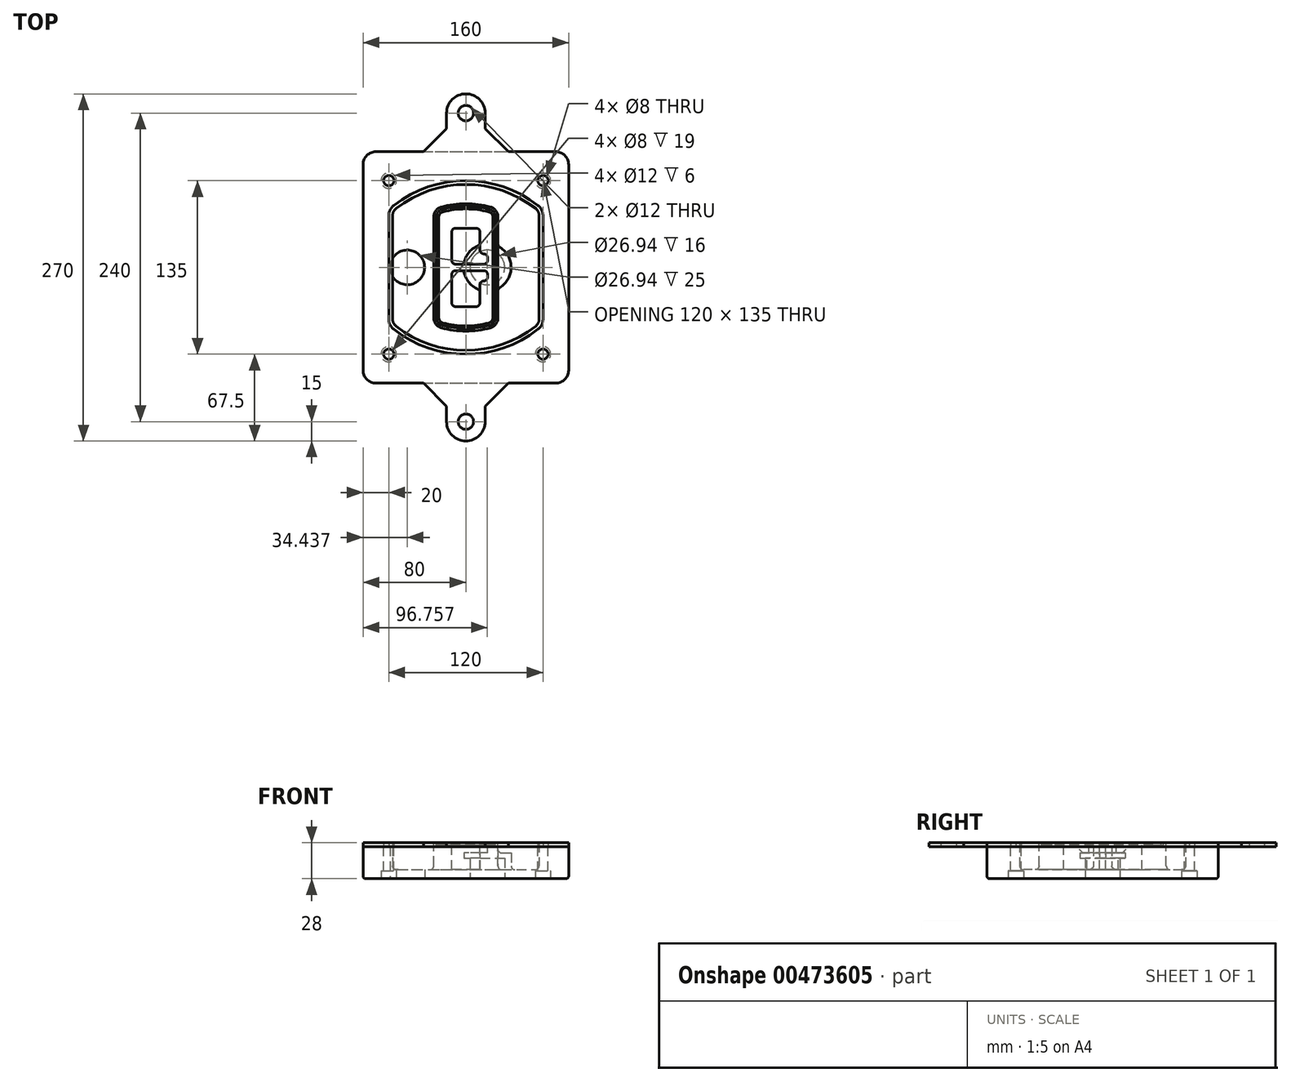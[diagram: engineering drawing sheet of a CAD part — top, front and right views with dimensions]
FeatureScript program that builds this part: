
annotation { "Feature Type Name" : "Feature", "Feature Type Description" : "" }
export const myFeature = defineFeature(function(context is Context, id is Id, definition is map)
    precondition{}
    {
        {
            var Q0;
            Q0=qCreatedBy(makeId("Top.planeOp"),FACE);
            var sketch = newSketch(context, id + "F0", { "sketchPlane" : qUnion([Q0])});
            skPoint(sketch, "E0.rect.middle", {"position": v(0, 0) * mm});
            skLineSegment(sketch, "E1.bottom", {"start": v(-70, -90) * mm, "end": v(70, -90) * mm});
            skLineSegment(sketch, "E1.top", {"start": v(-70, 90) * mm, "end": v(70, 90) * mm});
            skLineSegment(sketch, "E1.left", {"start": v(-80, -80) * mm, "end": v(-80, 80) * mm});
            skLineSegment(sketch, "E1.right", {"start": v(80, -80) * mm, "end": v(80, 80) * mm});
            skLineSegment(sketch, "E2", {"start": v(-80, 90) * mm, "end": v(80, -90) * mm, "construction": true});
            skLineSegment(sketch, "E3", {"start": v(80, 90) * mm, "end": v(-80, -90) * mm, "construction": true});
            skCircle(sketch, "E4", {"center": v(-60, 67.5) * mm, "radius": 4 * mm});
            skCircle(sketch, "E5", {"center": v(60, 67.5) * mm, "radius": 4 * mm});
            skCircle(sketch, "E6", {"center": v(60, -67.5) * mm, "radius": 4 * mm});
            skCircle(sketch, "E7", {"center": v(-60, -67.5) * mm, "radius": 4 * mm});
            skLineSegment(sketch, "E8", {"start": v(-60, 67.5) * mm, "end": v(60, 67.5) * mm, "construction": true});
            skLineSegment(sketch, "E9", {"start": v(60, 67.5) * mm, "end": v(60, -67.5) * mm, "construction": true});
            skLineSegment(sketch, "E10", {"start": v(60, -67.5) * mm, "end": v(-60, -67.5) * mm, "construction": true});
            skLineSegment(sketch, "E11", {"start": v(-60, -67.5) * mm, "end": v(-60, 67.5) * mm, "construction": true});
            skLineSegment(sketch, "E12", {"start": v(-60, 40.3) * mm, "end": v(-60, -40.3) * mm});
            skLineSegment(sketch, "E13", {"start": v(60, 40.3) * mm, "end": v(60, -40.3) * mm});
            skArc(sketch, "E14", {"start": v(56.15, 48.18) * mm, "mid": v(0, 67.5) * mm, "end": v(-56.15, 48.18) * mm});
            skArc(sketch, "E15", {"start": v(-56.15, -48.18) * mm, "mid": v(0, -67.5) * mm, "end": v(56.15, -48.18) * mm});
            skLineSegment(sketch, "E16", {"start": v(-60, 0) * mm, "end": v(60, 0) * mm, "construction": true});
            skPoint(sketch, "E17.visualSharp", {"position": v(-60, -45) * mm});
            skArc(sketch, "E17.filletArc", {"start": v(-60, -40.3) * mm, "mid": v(-58.99, -44.68) * mm, "end": v(-56.15, -48.18) * mm});
            skPoint(sketch, "E18.visualSharp", {"position": v(-60, 45) * mm});
            skArc(sketch, "E18.filletArc", {"start": v(-56.15, 48.18) * mm, "mid": v(-58.99, 44.68) * mm, "end": v(-60, 40.3) * mm});
            skPoint(sketch, "E19.visualSharp", {"position": v(60, 45) * mm});
            skArc(sketch, "E19.filletArc", {"start": v(60, 40.3) * mm, "mid": v(58.99, 44.68) * mm, "end": v(56.15, 48.18) * mm});
            skPoint(sketch, "E20.visualSharp", {"position": v(60, -45) * mm});
            skArc(sketch, "E20.filletArc", {"start": v(56.15, -48.18) * mm, "mid": v(58.99, -44.68) * mm, "end": v(60, -40.3) * mm});
            skPoint(sketch, "E21.visualSharp", {"position": v(-80, 90) * mm});
            skArc(sketch, "E21.filletArc", {"start": v(-70, 90) * mm, "mid": v(-77.07, 87.07) * mm, "end": v(-80, 80) * mm});
            skPoint(sketch, "E22.visualSharp", {"position": v(80, 90) * mm});
            skArc(sketch, "E22.filletArc", {"start": v(80, 80) * mm, "mid": v(77.07, 87.07) * mm, "end": v(70, 90) * mm});
            skPoint(sketch, "E23.visualSharp", {"position": v(80, -90) * mm});
            skArc(sketch, "E23.filletArc", {"start": v(70, -90) * mm, "mid": v(77.07, -87.07) * mm, "end": v(80, -80) * mm});
            skPoint(sketch, "E24.visualSharp", {"position": v(-80, -90) * mm});
            skArc(sketch, "E24.filletArc", {"start": v(-80, -80) * mm, "mid": v(-77.07, -87.07) * mm, "end": v(-70, -90) * mm});
            skArc(sketch, "E25.0", {"start": v(57, 40.3) * mm, "mid": v(56.3, 43.36) * mm, "end": v(54.3, 45.81) * mm});
            skLineSegment(sketch, "E25.1", {"start": v(57, 40.3) * mm, "end": v(57, -40.3) * mm});
            skArc(sketch, "E25.2", {"start": v(54.3, -45.81) * mm, "mid": v(56.3, -43.36) * mm, "end": v(57, -40.3) * mm});
            skArc(sketch, "E25.3", {"start": v(-54.3, -45.81) * mm, "mid": v(0, -64.5) * mm, "end": v(54.3, -45.81) * mm});
            skArc(sketch, "E25.4", {"start": v(-57, -40.3) * mm, "mid": v(-56.3, -43.36) * mm, "end": v(-54.3, -45.81) * mm});
            skArc(sketch, "E25.5", {"start": v(54.3, 45.81) * mm, "mid": v(0, 64.5) * mm, "end": v(-54.3, 45.81) * mm});
            skLineSegment(sketch, "E25.6", {"start": v(-57, 40.3) * mm, "end": v(-57, -40.3) * mm});
            skArc(sketch, "E25.7", {"start": v(-54.3, 45.81) * mm, "mid": v(-56.3, 43.36) * mm, "end": v(-57, 40.3) * mm});
            skArc(sketch, "E26.0", {"start": v(-58.62, 51.33) * mm, "mid": v(-62.58, 46.43) * mm, "end": v(-64, 40.3) * mm});
            skArc(sketch, "E26.1", {"start": v(58.62, 51.33) * mm, "mid": v(0, 71.5) * mm, "end": v(-58.62, 51.33) * mm});
            skArc(sketch, "E26.2", {"start": v(64, 40.3) * mm, "mid": v(62.58, 46.43) * mm, "end": v(58.62, 51.33) * mm});
            skLineSegment(sketch, "E26.3", {"start": v(64, 40.3) * mm, "end": v(64, -40.3) * mm});
            skArc(sketch, "E26.4", {"start": v(58.62, -51.33) * mm, "mid": v(62.58, -46.43) * mm, "end": v(64, -40.3) * mm});
            skLineSegment(sketch, "E26.5", {"start": v(-64, 40.3) * mm, "end": v(-64, -40.3) * mm});
            skArc(sketch, "E26.6", {"start": v(-58.62, -51.33) * mm, "mid": v(0, -71.5) * mm, "end": v(58.62, -51.33) * mm});
            skArc(sketch, "E26.7", {"start": v(-64, -40.3) * mm, "mid": v(-62.58, -46.43) * mm, "end": v(-58.62, -51.33) * mm});
            skSolve(sketch);
        }
        {
            var Q0;
            Q0=makeQuery(id+"F0.imprint","IMPRINT",FACE,{"disambiguationData":[TD([[makeQuery(id+"F0.imprint","IMPRINT",EDGE,{"derivedFrom":sQuery(id+"F0.wireOp",EDGE,"E1.bottom")}),1.0]])]});
            var Q1;
            Q1=makeQuery(id+"F0.imprint","IMPRINT",FACE,{"disambiguationData":[TD([[makeQuery(id+"F0.imprint","IMPRINT",EDGE,{"derivedFrom":sQuery(id+"F0.wireOp",EDGE,"E12")}),1.0]])]});
            var Q2;
            Q2=makeQuery(id+"F0.imprint","IMPRINT",FACE,{"disambiguationData":[TD([[makeQuery(id+"F0.imprint","IMPRINT",EDGE,{"derivedFrom":sQuery(id+"F0.wireOp",EDGE,"E25.0")}),1.0]])]});
            var Q3;
            Q3=makeQuery(id+"F0.imprint","IMPRINT",FACE,{"disambiguationData":[TD([[makeQuery(id+"F0.imprint","IMPRINT",EDGE,{"derivedFrom":sQuery(id+"F0.wireOp",EDGE,"E12")}),-1.0]])]});
            extrude(context, id + "F1", {"entities" : qUnion([Q0, Q1, Q2, Q3]), "oppositeDirection" : true, "depth" : 25 * mm});
        }
        {
            var Q0;
            Q0=makeQuery(id+"F0.imprint","IMPRINT",FACE,{"disambiguationData":[TD([[makeQuery(id+"F0.imprint","IMPRINT",EDGE,{"derivedFrom":sQuery(id+"F0.wireOp",EDGE,"E12")}),1.0]])]});
            extrude(context, id + "F2", {"entities" : qUnion([Q0]), "operationType" : NewBodyOperationType.ADD, "depth" : 3 * mm});
        }
        {
            var Q0;
            Q0=makeQuery(id+"F0.imprint","IMPRINT",FACE,{"disambiguationData":[TD([[makeQuery(id+"F0.imprint","IMPRINT",EDGE,{"derivedFrom":sQuery(id+"F0.wireOp",EDGE,"E25.0")}),1.0]])]});
            extrude(context, id + "F3", {"entities" : qUnion([Q0]), "operationType" : NewBodyOperationType.REMOVE, "oppositeDirection" : true, "depth" : 18 * mm});
        }
        {
            var Q0;
            Q0=makeQuery(id+"F2.opExtrude","CAP_FACE",FACE,{"disambiguationData":[OSD([sQuery(id+"F0.wireOp",EDGE,"E12"),sQuery(id+"F0.wireOp",EDGE,"E13"),sQuery(id+"F0.wireOp",EDGE,"E14"),sQuery(id+"F0.wireOp",EDGE,"E15"),sQuery(id+"F0.wireOp",EDGE,"E17.filletArc"),sQuery(id+"F0.wireOp",EDGE,"E18.filletArc"),sQuery(id+"F0.wireOp",EDGE,"E19.filletArc"),sQuery(id+"F0.wireOp",EDGE,"E20.filletArc"),sQuery(id+"F0.wireOp",EDGE,"E25.0"),sQuery(id+"F0.wireOp",EDGE,"E25.1"),sQuery(id+"F0.wireOp",EDGE,"E25.2"),sQuery(id+"F0.wireOp",EDGE,"E25.3"),sQuery(id+"F0.wireOp",EDGE,"E25.4"),sQuery(id+"F0.wireOp",EDGE,"E25.5"),sQuery(id+"F0.wireOp",EDGE,"E25.6"),sQuery(id+"F0.wireOp",EDGE,"E25.7")])],"isStart":false});
            var sketch = newSketch(context, id + "F4", { "sketchPlane" : qUnion([Q0])});
            skArc(sketch, "E27.0", {"start": v(-19.08, -46.97) * mm, "mid": v(0, -49.5) * mm, "end": v(19.08, -46.97) * mm});
            skArc(sketch, "E28.0", {"start": v(19.08, 46.97) * mm, "mid": v(0, 49.5) * mm, "end": v(-19.08, 46.97) * mm});
            skLineSegment(sketch, "E29", {"start": v(-25, 39.25) * mm, "end": v(-25, -39.25) * mm});
            skLineSegment(sketch, "E30", {"start": v(25, 39.25) * mm, "end": v(25, -39.25) * mm});
            skLineSegment(sketch, "E31", {"start": v(-25, 45.1) * mm, "end": v(25, 45.1) * mm, "construction": true});
            skLineSegment(sketch, "E32", {"start": v(-25, -45.1) * mm, "end": v(25, -45.1) * mm, "construction": true});
            skPoint(sketch, "E33.visualSharp", {"position": v(-25, 45.1) * mm});
            skArc(sketch, "E33.filletArc", {"start": v(-19.08, 46.97) * mm, "mid": v(-23.35, 44.11) * mm, "end": v(-25, 39.25) * mm});
            skPoint(sketch, "E34.visualSharp", {"position": v(25, 45.1) * mm});
            skArc(sketch, "E34.filletArc", {"start": v(25, 39.25) * mm, "mid": v(23.35, 44.11) * mm, "end": v(19.08, 46.97) * mm});
            skPoint(sketch, "E35.visualSharp", {"position": v(25, -45.1) * mm});
            skArc(sketch, "E35.filletArc", {"start": v(19.08, -46.97) * mm, "mid": v(23.35, -44.11) * mm, "end": v(25, -39.25) * mm});
            skPoint(sketch, "E36.visualSharp", {"position": v(-25, -45.1) * mm});
            skArc(sketch, "E36.filletArc", {"start": v(-25, -39.25) * mm, "mid": v(-23.35, -44.11) * mm, "end": v(-19.08, -46.97) * mm});
            skArc(sketch, "E37.0", {"start": v(54.3, 45.81) * mm, "mid": v(0, 64.5) * mm, "end": v(-54.3, 45.81) * mm});
            skArc(sketch, "E37.1", {"start": v(-54.3, 45.81) * mm, "mid": v(-56.3, 43.36) * mm, "end": v(-57, 40.3) * mm});
            skLineSegment(sketch, "E37.2", {"start": v(-57, 40.3) * mm, "end": v(-57, -40.3) * mm});
            skArc(sketch, "E37.3", {"start": v(-57, -40.3) * mm, "mid": v(-56.3, -43.36) * mm, "end": v(-54.3, -45.81) * mm});
            skArc(sketch, "E37.4", {"start": v(-54.3, -45.81) * mm, "mid": v(0, -64.5) * mm, "end": v(54.3, -45.81) * mm});
            skArc(sketch, "E37.5", {"start": v(54.3, -45.81) * mm, "mid": v(56.3, -43.36) * mm, "end": v(57, -40.3) * mm});
            skLineSegment(sketch, "E37.6", {"start": v(57, 40.3) * mm, "end": v(57, -40.3) * mm});
            skArc(sketch, "E37.7", {"start": v(57, 40.3) * mm, "mid": v(56.3, 43.36) * mm, "end": v(54.3, 45.81) * mm});
            skLineSegment(sketch, "E38.0", {"start": v(23, 39.25) * mm, "end": v(23, -39.25) * mm});
            skArc(sketch, "E38.1", {"start": v(18.56, -45.04) * mm, "mid": v(21.76, -42.9) * mm, "end": v(23, -39.25) * mm});
            skArc(sketch, "E38.2", {"start": v(-18.56, -45.04) * mm, "mid": v(0, -47.5) * mm, "end": v(18.56, -45.04) * mm});
            skArc(sketch, "E38.3", {"start": v(-23, -39.25) * mm, "mid": v(-21.76, -42.9) * mm, "end": v(-18.56, -45.04) * mm});
            skLineSegment(sketch, "E38.4", {"start": v(-23, 39.25) * mm, "end": v(-23, -39.25) * mm});
            skArc(sketch, "E38.5", {"start": v(23, 39.25) * mm, "mid": v(21.76, 42.9) * mm, "end": v(18.56, 45.04) * mm});
            skArc(sketch, "E38.6", {"start": v(-18.56, 45.04) * mm, "mid": v(-21.76, 42.9) * mm, "end": v(-23, 39.25) * mm});
            skArc(sketch, "E38.7", {"start": v(18.56, 45.04) * mm, "mid": v(0, 47.5) * mm, "end": v(-18.56, 45.04) * mm});
            skArc(sketch, "E39.0", {"start": v(21, 39.25) * mm, "mid": v(20.18, 41.68) * mm, "end": v(18.04, 43.1) * mm});
            skLineSegment(sketch, "E39.1", {"start": v(21, 39.25) * mm, "end": v(21, -39.25) * mm});
            skArc(sketch, "E39.2", {"start": v(18.04, -43.1) * mm, "mid": v(20.18, -41.68) * mm, "end": v(21, -39.25) * mm});
            skArc(sketch, "E39.3", {"start": v(-18.04, -43.1) * mm, "mid": v(0, -45.5) * mm, "end": v(18.04, -43.1) * mm});
            skArc(sketch, "E39.4", {"start": v(-21, -39.25) * mm, "mid": v(-20.18, -41.68) * mm, "end": v(-18.04, -43.1) * mm});
            skArc(sketch, "E39.5", {"start": v(18.04, 43.1) * mm, "mid": v(0, 45.5) * mm, "end": v(-18.04, 43.1) * mm});
            skLineSegment(sketch, "E39.6", {"start": v(-21, 39.25) * mm, "end": v(-21, -39.25) * mm});
            skArc(sketch, "E39.7", {"start": v(-18.04, 43.1) * mm, "mid": v(-20.18, 41.68) * mm, "end": v(-21, 39.25) * mm});
            skLineSegment(sketch, "E40", {"start": v(-25, 0) * mm, "end": v(25, 0) * mm, "construction": true});
            skLineSegment(sketch, "E41", {"start": v(-11, 5.5) * mm, "end": v(-11, 27.5) * mm});
            skLineSegment(sketch, "E42", {"start": v(-8, 30.5) * mm, "end": v(8, 30.5) * mm});
            skLineSegment(sketch, "E43", {"start": v(11, 27.5) * mm, "end": v(11, 13.5) * mm});
            skLineSegment(sketch, "E44", {"start": v(14, 10.5) * mm, "end": v(14, 10.5) * mm});
            skLineSegment(sketch, "E45", {"start": v(17, 7.5) * mm, "end": v(17, 5.5) * mm});
            skLineSegment(sketch, "E46", {"start": v(14, 2.5) * mm, "end": v(-8, 2.5) * mm});
            skPoint(sketch, "E47.visualSharp", {"position": v(-11, 30.5) * mm});
            skArc(sketch, "E47.filletArc", {"start": v(-8, 30.5) * mm, "mid": v(-10.12, 29.62) * mm, "end": v(-11, 27.5) * mm});
            skPoint(sketch, "E48.visualSharp", {"position": v(11, 30.5) * mm});
            skArc(sketch, "E48.filletArc", {"start": v(11, 27.5) * mm, "mid": v(10.12, 29.62) * mm, "end": v(8, 30.5) * mm});
            skPoint(sketch, "E49.visualSharp", {"position": v(11, 10.5) * mm});
            skArc(sketch, "E49.filletArc", {"start": v(11, 13.5) * mm, "mid": v(11.88, 11.38) * mm, "end": v(14, 10.5) * mm});
            skPoint(sketch, "E50.visualSharp", {"position": v(17, 10.5) * mm});
            skArc(sketch, "E50.filletArc", {"start": v(17, 7.5) * mm, "mid": v(16.12, 9.62) * mm, "end": v(14, 10.5) * mm});
            skPoint(sketch, "E51.visualSharp", {"position": v(17, 2.5) * mm});
            skArc(sketch, "E51.filletArc", {"start": v(14, 2.5) * mm, "mid": v(16.12, 3.38) * mm, "end": v(17, 5.5) * mm});
            skPoint(sketch, "E52.visualSharp", {"position": v(-11, 2.5) * mm});
            skArc(sketch, "E52.filletArc", {"start": v(-11, 5.5) * mm, "mid": v(-10.12, 3.38) * mm, "end": v(-8, 2.5) * mm});
            skLineSegment(sketch, "E53.0.MirrorCS", {"start": v(14, -2.5) * mm, "end": v(-8, -2.5) * mm});
            skArc(sketch, "E54.0.MirrorCS", {"start": v(-11, -5.5) * mm, "mid": v(-10.12, -3.38) * mm, "end": v(-8, -2.5) * mm});
            skLineSegment(sketch, "E55.0.MirrorCS", {"start": v(-11, -5.5) * mm, "end": v(-11, -27.5) * mm});
            skArc(sketch, "E56.0.MirrorCS", {"start": v(-8, -30.5) * mm, "mid": v(-10.12, -29.62) * mm, "end": v(-11, -27.5) * mm});
            skLineSegment(sketch, "E57.0.MirrorCS", {"start": v(-8, -30.5) * mm, "end": v(8, -30.5) * mm});
            skArc(sketch, "E58.0.MirrorCS", {"start": v(11, -27.5) * mm, "mid": v(10.12, -29.62) * mm, "end": v(8, -30.5) * mm});
            skLineSegment(sketch, "E59.0.MirrorCS", {"start": v(11, -27.5) * mm, "end": v(11, -13.5) * mm});
            skArc(sketch, "E60.0.MirrorCS", {"start": v(11, -13.5) * mm, "mid": v(11.88, -11.38) * mm, "end": v(14, -10.5) * mm});
            skArc(sketch, "E61.0.MirrorCS", {"start": v(17, -7.5) * mm, "mid": v(16.12, -9.62) * mm, "end": v(14, -10.5) * mm});
            skLineSegment(sketch, "E62.0.MirrorCS", {"start": v(17, -7.5) * mm, "end": v(17, -5.5) * mm});
            skArc(sketch, "E63.0.MirrorCS", {"start": v(14, -2.5) * mm, "mid": v(16.12, -3.38) * mm, "end": v(17, -5.5) * mm});
            skSolve(sketch);
        }
        {
            var Q0;
            Q0=makeQuery(id+"F4.imprint","IMPRINT",FACE,{"disambiguationData":[TD([[makeQuery(id+"F4.imprint","IMPRINT",EDGE,{"derivedFrom":sQuery(id+"F4.wireOp",EDGE,"E27.0")}),1.0]])]});
            var Q1;
            Q1=makeQuery(id+"F4.imprint","IMPRINT",FACE,{"disambiguationData":[TD([[makeQuery(id+"F4.imprint","IMPRINT",EDGE,{"derivedFrom":sQuery(id+"F4.wireOp",EDGE,"E38.0")}),-1.0]])]});
            var Q2;
            Q2=makeQuery(id+"F4.imprint","IMPRINT",FACE,{"disambiguationData":[TD([[makeQuery(id+"F4.imprint","IMPRINT",EDGE,{"derivedFrom":sQuery(id+"F4.wireOp",EDGE,"E39.0")}),1.0]])]});
            extrude(context, id + "F5", {"entities" : qUnion([Q0, Q1, Q2]), "operationType" : NewBodyOperationType.ADD, "endBound" : BoundingType.UP_TO_NEXT, "oppositeDirection" : true, "depth" : 25 * mm});
        }
        {
            var Q0;
            Q0=makeQuery(id+"F4.imprint","IMPRINT",FACE,{"disambiguationData":[TD([[makeQuery(id+"F4.imprint","IMPRINT",EDGE,{"derivedFrom":sQuery(id+"F4.wireOp",EDGE,"E38.0")}),-1.0]])]});
            extrude(context, id + "F6", {"entities" : qUnion([Q0]), "operationType" : NewBodyOperationType.REMOVE, "oppositeDirection" : true, "depth" : 2 * mm});
        }
        {
            var Q0;
            Q0=makeQuery(id+"F1.opExtrude","CAP_FACE",FACE,{"disambiguationData":[OSD([sQuery(id+"F0.wireOp",EDGE,"E1.bottom"),sQuery(id+"F0.wireOp",EDGE,"E1.top"),sQuery(id+"F0.wireOp",EDGE,"E1.left"),sQuery(id+"F0.wireOp",EDGE,"E1.right"),sQuery(id+"F0.wireOp",EDGE,"E4"),sQuery(id+"F0.wireOp",EDGE,"E5"),sQuery(id+"F0.wireOp",EDGE,"E6"),sQuery(id+"F0.wireOp",EDGE,"E7"),sQuery(id+"F0.wireOp",EDGE,"E21.filletArc"),sQuery(id+"F0.wireOp",EDGE,"E22.filletArc"),sQuery(id+"F0.wireOp",EDGE,"E23.filletArc"),sQuery(id+"F0.wireOp",EDGE,"E24.filletArc")])],"isStart":false});
            var sketch = newSketch(context, id + "F7", { "sketchPlane" : qUnion([Q0])});
            skCircle(sketch, "E64", {"center": v(16.76, 0) * mm, "radius": 13.47 * mm});
            skCircle(sketch, "E65", {"center": v(-45.56, 0) * mm, "radius": 13.47 * mm});
            skLineSegment(sketch, "E66", {"start": v(80, 0) * mm, "end": v(-80, 0) * mm});
            skCircle(sketch, "E67", {"center": v(16.76, 0) * mm, "radius": 18.47 * mm});
            skCircle(sketch, "E68", {"center": v(60, -67.5) * mm, "radius": 6 * mm});
            skCircle(sketch, "E69", {"center": v(-60, -67.5) * mm, "radius": 6 * mm});
            skCircle(sketch, "E70", {"center": v(-60, 67.5) * mm, "radius": 6 * mm});
            skCircle(sketch, "E71", {"center": v(60, 67.5) * mm, "radius": 6 * mm});
            skSolve(sketch);
        }
        {
            var Q0;
            {var subQ1=sQuery(id+"F7.wireOp",EDGE,"E66");var subQ4=sQuery(id+"F7.wireOp",EDGE,"E64");var subQ6=makeQuery(id+"F7.imprint","INTERSECT",VERTEX,{"disambiguationData":[OD(0.0)],"derivedFrom":[subQ4,subQ1]});Q0=makeQuery(id+"F7.imprint","IMPRINT",FACE,{"disambiguationData":[TD([[makeQuery(id+"F7.imprint","IMPRINT",EDGE,{"disambiguationData":[TD([[subQ6,-1.0]])],"derivedFrom":subQ4}),-1.0]])]});}
            var Q1;
            {var subQ0=sQuery(id+"F7.wireOp",EDGE,"E66");var subQ1=sQuery(id+"F7.wireOp",EDGE,"E64");var subQ3=makeQuery(id+"F7.imprint","INTERSECT",VERTEX,{"disambiguationData":[OD(0.0)],"derivedFrom":[subQ1,subQ0]});Q1=makeQuery(id+"F7.imprint","IMPRINT",FACE,{"disambiguationData":[TD([[makeQuery(id+"F7.imprint","IMPRINT",EDGE,{"disambiguationData":[TD([[subQ3,-1.0]])],"derivedFrom":subQ1}),1.0]])]});}
            var Q2;
            {var subQ0=sQuery(id+"F7.wireOp",EDGE,"E66");var subQ1=sQuery(id+"F7.wireOp",EDGE,"E64");var subQ3=makeQuery(id+"F7.imprint","INTERSECT",VERTEX,{"disambiguationData":[OD(0.0)],"derivedFrom":[subQ1,subQ0]});Q2=makeQuery(id+"F7.imprint","IMPRINT",FACE,{"disambiguationData":[TD([[makeQuery(id+"F7.imprint","IMPRINT",EDGE,{"disambiguationData":[TD([[subQ3,1.0]])],"derivedFrom":subQ1}),1.0]])]});}
            var Q3;
            {var subQ1=sQuery(id+"F7.wireOp",EDGE,"E66");var subQ4=sQuery(id+"F7.wireOp",EDGE,"E64");var subQ6=makeQuery(id+"F7.imprint","INTERSECT",VERTEX,{"disambiguationData":[OD(0.0)],"derivedFrom":[subQ4,subQ1]});Q3=makeQuery(id+"F7.imprint","IMPRINT",FACE,{"disambiguationData":[TD([[makeQuery(id+"F7.imprint","IMPRINT",EDGE,{"disambiguationData":[TD([[subQ6,1.0]])],"derivedFrom":subQ4}),-1.0]])]});}
            extrude(context, id + "F8", {"entities" : qUnion([Q0, Q1, Q2, Q3]), "operationType" : NewBodyOperationType.ADD, "oppositeDirection" : true, "depth" : 20 * mm});
        }
        {
            var Q0;
            {var subQ0=sQuery(id+"F7.wireOp",EDGE,"E66");var subQ1=sQuery(id+"F7.wireOp",EDGE,"E64");var subQ3=makeQuery(id+"F7.imprint","INTERSECT",VERTEX,{"disambiguationData":[OD(0.0)],"derivedFrom":[subQ1,subQ0]});Q0=makeQuery(id+"F7.imprint","IMPRINT",FACE,{"disambiguationData":[TD([[makeQuery(id+"F7.imprint","IMPRINT",EDGE,{"disambiguationData":[TD([[subQ3,-1.0]])],"derivedFrom":subQ1}),1.0]])]});}
            var Q1;
            {var subQ0=sQuery(id+"F7.wireOp",EDGE,"E66");var subQ1=sQuery(id+"F7.wireOp",EDGE,"E64");var subQ3=makeQuery(id+"F7.imprint","INTERSECT",VERTEX,{"disambiguationData":[OD(0.0)],"derivedFrom":[subQ1,subQ0]});Q1=makeQuery(id+"F7.imprint","IMPRINT",FACE,{"disambiguationData":[TD([[makeQuery(id+"F7.imprint","IMPRINT",EDGE,{"disambiguationData":[TD([[subQ3,1.0]])],"derivedFrom":subQ1}),1.0]])]});}
            extrude(context, id + "F9", {"entities" : qUnion([Q0, Q1]), "operationType" : NewBodyOperationType.REMOVE, "oppositeDirection" : true, "depth" : 16 * mm});
        }
        {
            var Q0;
            {var subQ0=sQuery(id+"F7.wireOp",EDGE,"E66");var subQ1=sQuery(id+"F7.wireOp",EDGE,"E65");var subQ3=makeQuery(id+"F7.imprint","INTERSECT",VERTEX,{"disambiguationData":[OD(0.0)],"derivedFrom":[subQ1,subQ0]});Q0=makeQuery(id+"F7.imprint","IMPRINT",FACE,{"disambiguationData":[TD([[makeQuery(id+"F7.imprint","IMPRINT",EDGE,{"disambiguationData":[TD([[subQ3,-1.0]])],"derivedFrom":subQ1}),1.0]])]});}
            var Q1;
            {var subQ0=sQuery(id+"F7.wireOp",EDGE,"E66");var subQ1=sQuery(id+"F7.wireOp",EDGE,"E65");var subQ3=makeQuery(id+"F7.imprint","INTERSECT",VERTEX,{"disambiguationData":[OD(0.0)],"derivedFrom":[subQ1,subQ0]});Q1=makeQuery(id+"F7.imprint","IMPRINT",FACE,{"disambiguationData":[TD([[makeQuery(id+"F7.imprint","IMPRINT",EDGE,{"disambiguationData":[TD([[subQ3,1.0]])],"derivedFrom":subQ1}),1.0]])]});}
            extrude(context, id + "F10", {"entities" : qUnion([Q0, Q1]), "operationType" : NewBodyOperationType.REMOVE, "oppositeDirection" : true, "depth" : 25 * mm});
        }
        {
            var Q0;
            Q0=makeQuery(id+"F7.imprint","IMPRINT",FACE,{"disambiguationData":[TD([[makeQuery(id+"F7.imprint","IMPRINT",EDGE,{"derivedFrom":sQuery(id+"F7.wireOp",EDGE,"E68")}),1.0]])]});
            var Q1;
            Q1=makeQuery(id+"F7.imprint","IMPRINT",FACE,{"disambiguationData":[TD([[makeQuery(id+"F7.imprint","IMPRINT",EDGE,{"derivedFrom":makeQuery(id+"F1.opExtrude","CAP_EDGE",EDGE,{"disambiguationData":[OSD([sQuery(id+"F0.wireOp",EDGE,"E5")])],"isStart":false})}),-1.0]])]});
            var Q2;
            Q2=makeQuery(id+"F7.imprint","IMPRINT",FACE,{"disambiguationData":[TD([[makeQuery(id+"F7.imprint","IMPRINT",EDGE,{"derivedFrom":sQuery(id+"F7.wireOp",EDGE,"E69")}),1.0]])]});
            var Q3;
            Q3=makeQuery(id+"F7.imprint","IMPRINT",FACE,{"disambiguationData":[TD([[makeQuery(id+"F7.imprint","IMPRINT",EDGE,{"derivedFrom":makeQuery(id+"F1.opExtrude","CAP_EDGE",EDGE,{"disambiguationData":[OSD([sQuery(id+"F0.wireOp",EDGE,"E4")])],"isStart":false})}),-1.0]])]});
            var Q4;
            Q4=makeQuery(id+"F7.imprint","IMPRINT",FACE,{"disambiguationData":[TD([[makeQuery(id+"F7.imprint","IMPRINT",EDGE,{"derivedFrom":sQuery(id+"F7.wireOp",EDGE,"E70")}),1.0]])]});
            var Q5;
            Q5=makeQuery(id+"F7.imprint","IMPRINT",FACE,{"disambiguationData":[TD([[makeQuery(id+"F7.imprint","IMPRINT",EDGE,{"derivedFrom":makeQuery(id+"F1.opExtrude","CAP_EDGE",EDGE,{"disambiguationData":[OSD([sQuery(id+"F0.wireOp",EDGE,"E7")])],"isStart":false})}),-1.0]])]});
            var Q6;
            Q6=makeQuery(id+"F7.imprint","IMPRINT",FACE,{"disambiguationData":[TD([[makeQuery(id+"F7.imprint","IMPRINT",EDGE,{"derivedFrom":sQuery(id+"F7.wireOp",EDGE,"E71")}),1.0]])]});
            var Q7;
            Q7=makeQuery(id+"F7.imprint","IMPRINT",FACE,{"disambiguationData":[TD([[makeQuery(id+"F7.imprint","IMPRINT",EDGE,{"derivedFrom":makeQuery(id+"F1.opExtrude","CAP_EDGE",EDGE,{"disambiguationData":[OSD([sQuery(id+"F0.wireOp",EDGE,"E6")])],"isStart":false})}),-1.0]])]});
            extrude(context, id + "F11", {"entities" : qUnion([Q0, Q1, Q2, Q3, Q4, Q5, Q6, Q7]), "operationType" : NewBodyOperationType.REMOVE, "oppositeDirection" : true, "depth" : 6 * mm});
        }
        {
            var Q0;
            Q0=makeQuery(id+"F9.boolean.opBoolean","COPY",FACE,{"derivedFrom":makeQuery(id+"F9.opExtrude","CAP_FACE",FACE,{"disambiguationData":[OSD([sQuery(id+"F7.wireOp",EDGE,"E64")])],"isStart":false})});
            var sketch = newSketch(context, id + "F12", { "sketchPlane" : qUnion([Q0])});
            skArc(sketch, "E72.0", {"start": v(11, 17.55) * mm, "mid": v(2.57, 11.82) * mm, "end": v(-1.54, 2.5) * mm});
            skArc(sketch, "E72.1", {"start": v(-1.54, -2.5) * mm, "mid": v(2.57, -11.82) * mm, "end": v(11, -17.55) * mm});
            skLineSegment(sketch, "E73", {"start": v(-1.54, -2.5) * mm, "end": v(14, -2.5) * mm});
            skLineSegment(sketch, "E74.0", {"start": v(14, 2.5) * mm, "end": v(-1.54, 2.5) * mm});
            skArc(sketch, "E74.1", {"start": v(14, 2.5) * mm, "mid": v(16.12, 3.38) * mm, "end": v(17, 5.5) * mm});
            skLineSegment(sketch, "E74.2", {"start": v(17, 7.5) * mm, "end": v(17, 5.5) * mm});
            skArc(sketch, "E74.3", {"start": v(17, 7.5) * mm, "mid": v(16.12, 9.62) * mm, "end": v(14, 10.5) * mm});
            skArc(sketch, "E74.4", {"start": v(11, 13.5) * mm, "mid": v(11.88, 11.38) * mm, "end": v(14, 10.5) * mm});
            skLineSegment(sketch, "E74.5", {"start": v(11, 17.55) * mm, "end": v(11, 13.5) * mm});
            skLineSegment(sketch, "E74.7", {"start": v(14, -2.5) * mm, "end": v(-1.54, -2.5) * mm});
            skArc(sketch, "E74.8", {"start": v(14, -2.5) * mm, "mid": v(16.12, -3.38) * mm, "end": v(17, -5.5) * mm});
            skLineSegment(sketch, "E74.9", {"start": v(17, -7.5) * mm, "end": v(17, -5.5) * mm});
            skArc(sketch, "E74.10", {"start": v(17, -7.5) * mm, "mid": v(16.12, -9.62) * mm, "end": v(14, -10.5) * mm});
            skArc(sketch, "E74.11", {"start": v(11, -13.5) * mm, "mid": v(11.88, -11.38) * mm, "end": v(14, -10.5) * mm});
            skLineSegment(sketch, "E74.12", {"start": v(11, -17.55) * mm, "end": v(11, -13.5) * mm});
            skPoint(sketch, "E75.orphan", {"position": v(11, -27.5) * mm});
            skPoint(sketch, "E76.orphan", {"position": v(-8, -2.5) * mm});
            skPoint(sketch, "E77.orphan", {"position": v(-8, 2.5) * mm});
            skPoint(sketch, "E78.orphan", {"position": v(11, 27.5) * mm});
            skSolve(sketch);
        }
        {
            var Q0;
            {var subQ7=sQuery(id+"F12.wireOp",EDGE,"E72.0");var subQ14=sQuery(id+"F12.wireOp",EDGE,"E72.1");var subQ16=sQuery(id+"F12.wireOp",EDGE,"E74.1");var subQ18=sQuery(id+"F12.wireOp",EDGE,"E74.8");Q0=qUnion([makeQuery(id+"F12.imprint","IMPRINT",FACE,{"disambiguationData":[TD([[makeQuery(id+"F12.imprint","IMPRINT",EDGE,{"derivedFrom":subQ7}),1.0]])]}),makeQuery(id+"F12.imprint","IMPRINT",FACE,{"disambiguationData":[TD([[makeQuery(id+"F12.imprint","IMPRINT",EDGE,{"derivedFrom":subQ14}),1.0]])]}),makeQuery(id+"F12.imprint","IMPRINT",FACE,{"disambiguationData":[TD([[makeQuery(id+"F12.imprint","IMPRINT",EDGE,{"derivedFrom":subQ16}),1.0]])]}),makeQuery(id+"F12.imprint","IMPRINT",FACE,{"disambiguationData":[TD([[makeQuery(id+"F12.imprint","IMPRINT",EDGE,{"derivedFrom":subQ18}),-1.0]])]})]);}
            var Q1;
            Q1=makeQuery(id+"F5.boolean.opBoolean","SPLIT",FACE,{"disambiguationData":[TD([makeQuery(id+"F5.opExtrude","SWEPT_FACE",FACE,{"disambiguationData":[OSD([sQuery(id+"F4.wireOp",EDGE,"E41")])]})])],"derivedFrom":makeQuery(id+"F3.boolean.opBoolean","COPY",FACE,{"derivedFrom":makeQuery(id+"F3.opExtrude","CAP_FACE",FACE,{"disambiguationData":[OSD([sQuery(id+"F0.wireOp",EDGE,"E25.0"),sQuery(id+"F0.wireOp",EDGE,"E25.1"),sQuery(id+"F0.wireOp",EDGE,"E25.2"),sQuery(id+"F0.wireOp",EDGE,"E25.3"),sQuery(id+"F0.wireOp",EDGE,"E25.4"),sQuery(id+"F0.wireOp",EDGE,"E25.5"),sQuery(id+"F0.wireOp",EDGE,"E25.6"),sQuery(id+"F0.wireOp",EDGE,"E25.7")])],"isStart":false})})});
            extrude(context, id + "F13", {"entities" : qUnion([Q0]), "operationType" : NewBodyOperationType.REMOVE, "endBound" : BoundingType.UP_TO_SURFACE, "endBoundEntityFace" : qUnion([Q1]), "depth" : 25 * mm});
        }
        {
            var Q0;
            Q0=makeQuery(id+"F3.boolean.opBoolean","COPY",EDGE,{"derivedFrom":makeQuery(id+"F3.opExtrude","CAP_EDGE",EDGE,{"disambiguationData":[OSD([sQuery(id+"F0.wireOp",EDGE,"E25.6")])],"isStart":false})});
            var Q1;
            Q1=makeQuery(id+"F8.boolean.opBoolean","INTERSECT",EDGE,{"derivedFrom":[makeQuery(id+"F5.opExtrude","SWEPT_FACE",FACE,{"disambiguationData":[OSD([sQuery(id+"F4.wireOp",EDGE,"E30")])]}),makeQuery(id+"F8.opExtrude","CAP_FACE",FACE,{"disambiguationData":[OSD([sQuery(id+"F7.wireOp",EDGE,"E67")])],"isStart":false})]});
            var Q2;
            Q2=makeQuery(id+"F8.boolean.opBoolean","INTERSECT",EDGE,{"disambiguationData":[OD(1.0)],"derivedFrom":[makeQuery(id+"F5.opExtrude","SWEPT_FACE",FACE,{"disambiguationData":[OSD([sQuery(id+"F4.wireOp",EDGE,"E30")])]}),makeQuery(id+"F8.opExtrude","SWEPT_FACE",FACE,{"disambiguationData":[OSD([sQuery(id+"F7.wireOp",EDGE,"E67")])]})]});
            var Q3;
            {var subQ0=sQuery(id+"F4.wireOp",EDGE,"E30");Q3=makeQuery(id+"F8.boolean.opBoolean","SPLIT",EDGE,{"disambiguationData":[TD([makeQuery(id+"F5.opExtrude","SWEPT_FACE",FACE,{"disambiguationData":[OSD([sQuery(id+"F4.wireOp",EDGE,"E35.filletArc")])]})])],"derivedFrom":makeQuery(id+"F5.opExtrude","CAP_EDGE",EDGE,{"disambiguationData":[OSD([subQ0])],"isStart":false})});}
            var Q4;
            {var subQ0=sQuery(id+"F0.wireOp",EDGE,"E25.7");var subQ1=sQuery(id+"F0.wireOp",EDGE,"E25.1");var subQ2=sQuery(id+"F0.wireOp",EDGE,"E25.6");var subQ3=sQuery(id+"F0.wireOp",EDGE,"E25.5");var subQ4=sQuery(id+"F0.wireOp",EDGE,"E25.4");var subQ5=sQuery(id+"F0.wireOp",EDGE,"E25.0");var subQ6=sQuery(id+"F0.wireOp",EDGE,"E25.2");var subQ7=sQuery(id+"F0.wireOp",EDGE,"E25.3");Q4=makeQuery(id+"F8.boolean.opBoolean","INTERSECT",EDGE,{"derivedFrom":[makeQuery(id+"F5.boolean.opBoolean","SPLIT",FACE,{"disambiguationData":[TD([makeQuery(id+"F2.opExtrude","SWEPT_FACE",FACE,{"disambiguationData":[OSD([subQ5])]})])],"derivedFrom":makeQuery(id+"F3.boolean.opBoolean","COPY",FACE,{"derivedFrom":makeQuery(id+"F3.opExtrude","CAP_FACE",FACE,{"disambiguationData":[OSD([subQ5,subQ1,subQ6,subQ7,subQ4,subQ3,subQ2,subQ0])],"isStart":false})})}),makeQuery(id+"F8.opExtrude","SWEPT_FACE",FACE,{"disambiguationData":[OSD([sQuery(id+"F7.wireOp",EDGE,"E67")])]})]});}
            var Q5;
            Q5=makeQuery(id+"F8.boolean.opBoolean","INTERSECT",EDGE,{"disambiguationData":[OD(0.0)],"derivedFrom":[makeQuery(id+"F5.opExtrude","SWEPT_FACE",FACE,{"disambiguationData":[OSD([sQuery(id+"F4.wireOp",EDGE,"E30")])]}),makeQuery(id+"F8.opExtrude","SWEPT_FACE",FACE,{"disambiguationData":[OSD([sQuery(id+"F7.wireOp",EDGE,"E67")])]})]});
            fillet(context, id + "F14", {"entities" : qUnion([Q0, Q1, Q2, Q3, Q4, Q5]), "radius" : 3 * mm, "tangentPropagation" : true, "allowEdgeOverflow" : false});
        }
        {
            var Q0;
            Q0=makeQuery(id+"F1.opExtrude","CAP_EDGE",EDGE,{"disambiguationData":[OSD([sQuery(id+"F0.wireOp",EDGE,"E1.bottom")])],"isStart":false});
            fillet(context, id + "F15", {"entities" : qUnion([Q0]), "radius" : 2 * mm, "tangentPropagation" : true, "allowEdgeOverflow" : false});
        }
        {
            var Q0;
            {var subQ0=sQuery(id+"F0.wireOp",EDGE,"E21.filletArc");var subQ1=sQuery(id+"F0.wireOp",EDGE,"E7");var subQ2=sQuery(id+"F0.wireOp",EDGE,"E6");var subQ3=sQuery(id+"F0.wireOp",EDGE,"E5");var subQ4=sQuery(id+"F0.wireOp",EDGE,"E4");var subQ5=sQuery(id+"F0.wireOp",EDGE,"E22.filletArc");var subQ6=sQuery(id+"F0.wireOp",EDGE,"E1.bottom");var subQ7=sQuery(id+"F0.wireOp",EDGE,"E1.right");var subQ8=sQuery(id+"F0.wireOp",EDGE,"E1.top");var subQ9=sQuery(id+"F0.wireOp",EDGE,"E1.left");var subQ10=sQuery(id+"F0.wireOp",EDGE,"E23.filletArc");var subQ11=sQuery(id+"F0.wireOp",EDGE,"E24.filletArc");Q0=makeQuery(id+"F2.boolean.opBoolean","SPLIT",FACE,{"disambiguationData":[TD([makeQuery(id+"F1.opExtrude","SWEPT_FACE",FACE,{"disambiguationData":[OSD([subQ6])]})])],"derivedFrom":makeQuery(id+"F1.opExtrude","CAP_FACE",FACE,{"disambiguationData":[OSD([subQ6,subQ8,subQ9,subQ7,subQ4,subQ3,subQ2,subQ1,subQ0,subQ5,subQ10,subQ11])],"isStart":true})});}
            var sketch = newSketch(context, id + "F16", { "sketchPlane" : qUnion([Q0])});
            skLineSegment(sketch, "E79", {"start": v(-80, 0) * mm, "end": v(80, 0) * mm, "construction": true});
            skLineSegment(sketch, "E80.MirrorCS", {"start": v(15, -120) * mm, "end": v(15, -108) * mm});
            skLineSegment(sketch, "E81.MirrorCS", {"start": v(-15, -120) * mm, "end": v(-15, -108) * mm});
            skLineSegment(sketch, "E82.MirrorCS", {"start": v(15, -108) * mm, "end": v(33, -90) * mm});
            skCircle(sketch, "E83.MirrorC", {"center": v(0, -120) * mm, "radius": 6 * mm});
            skLineSegment(sketch, "E84.MirrorCS", {"start": v(-15, -108) * mm, "end": v(-33, -90) * mm});
            skArc(sketch, "E85.MirrorCS", {"start": v(15, -120) * mm, "mid": v(0, -135) * mm, "end": v(-15, -120) * mm});
            skArc(sketch, "E86.MirrorCS", {"start": v(-15, -120) * mm, "mid": v(0, -135) * mm, "end": v(15, -120) * mm});
            skLineSegment(sketch, "E87.MirrorCS", {"start": v(0, -90) * mm, "end": v(0, -120) * mm, "construction": true});
            skLineSegment(sketch, "E88", {"start": v(0, 90) * mm, "end": v(0, 120) * mm, "construction": true});
            skLineSegment(sketch, "E89", {"start": v(-33, 90) * mm, "end": v(-15, 108) * mm});
            skLineSegment(sketch, "E90", {"start": v(-15, 108) * mm, "end": v(-15, 120) * mm});
            skArc(sketch, "E91", {"start": v(15, 120) * mm, "mid": v(0, 135) * mm, "end": v(-15, 120) * mm});
            skLineSegment(sketch, "E92", {"start": v(15, 120) * mm, "end": v(15, 108) * mm});
            skLineSegment(sketch, "E93", {"start": v(15, 108) * mm, "end": v(33, 90) * mm});
            skCircle(sketch, "E94", {"center": v(0, 120) * mm, "radius": 6 * mm});
            skLineSegment(sketch, "E95", {"start": v(-15, 120) * mm, "end": v(15, 120) * mm, "construction": true});
            skSolve(sketch);
        }
        {
            var Q0;
            Q0=makeQuery(id+"F16.imprint","IMPRINT",FACE,{"disambiguationData":[TD([[makeQuery(id+"F16.imprint","IMPRINT",EDGE,{"derivedFrom":sQuery(id+"F16.wireOp",EDGE,"E80.MirrorCS")}),1.0]])]});
            var Q1;
            {var subQ0=sQuery(id+"F16.wireOp",EDGE,"E89");Q1=makeQuery(id+"F16.imprint","IMPRINT",FACE,{"disambiguationData":[TD([[makeQuery(id+"F16.imprint","IMPRINT",EDGE,{"derivedFrom":subQ0}),-1.0]])]});}
            var Q2;
            Q2=makeQuery(id+"F16.imprint","IMPRINT",FACE,{"disambiguationData":[TD([[makeQuery(id+"F16.imprint","IMPRINT",EDGE,{"derivedFrom":makeQuery(id+"F1.opExtrude","CAP_EDGE",EDGE,{"disambiguationData":[OSD([sQuery(id+"F0.wireOp",EDGE,"E1.left")])],"isStart":true})}),-1.0]])]});
            var Q3;
            Q3=makeQuery(id+"F2.opExtrude","CAP_FACE",FACE,{"disambiguationData":[OSD([sQuery(id+"F0.wireOp",EDGE,"E12"),sQuery(id+"F0.wireOp",EDGE,"E13"),sQuery(id+"F0.wireOp",EDGE,"E14"),sQuery(id+"F0.wireOp",EDGE,"E15"),sQuery(id+"F0.wireOp",EDGE,"E17.filletArc"),sQuery(id+"F0.wireOp",EDGE,"E18.filletArc"),sQuery(id+"F0.wireOp",EDGE,"E19.filletArc"),sQuery(id+"F0.wireOp",EDGE,"E20.filletArc"),sQuery(id+"F0.wireOp",EDGE,"E25.0"),sQuery(id+"F0.wireOp",EDGE,"E25.1"),sQuery(id+"F0.wireOp",EDGE,"E25.2"),sQuery(id+"F0.wireOp",EDGE,"E25.3"),sQuery(id+"F0.wireOp",EDGE,"E25.4"),sQuery(id+"F0.wireOp",EDGE,"E25.5"),sQuery(id+"F0.wireOp",EDGE,"E25.6"),sQuery(id+"F0.wireOp",EDGE,"E25.7")])],"isStart":false});
            extrude(context, id + "F17", {"entities" : qUnion([Q0, Q1, Q2]), "endBound" : BoundingType.UP_TO_SURFACE, "endBoundEntityFace" : qUnion([Q3]), "depth" : 25 * mm});
        }
    });
